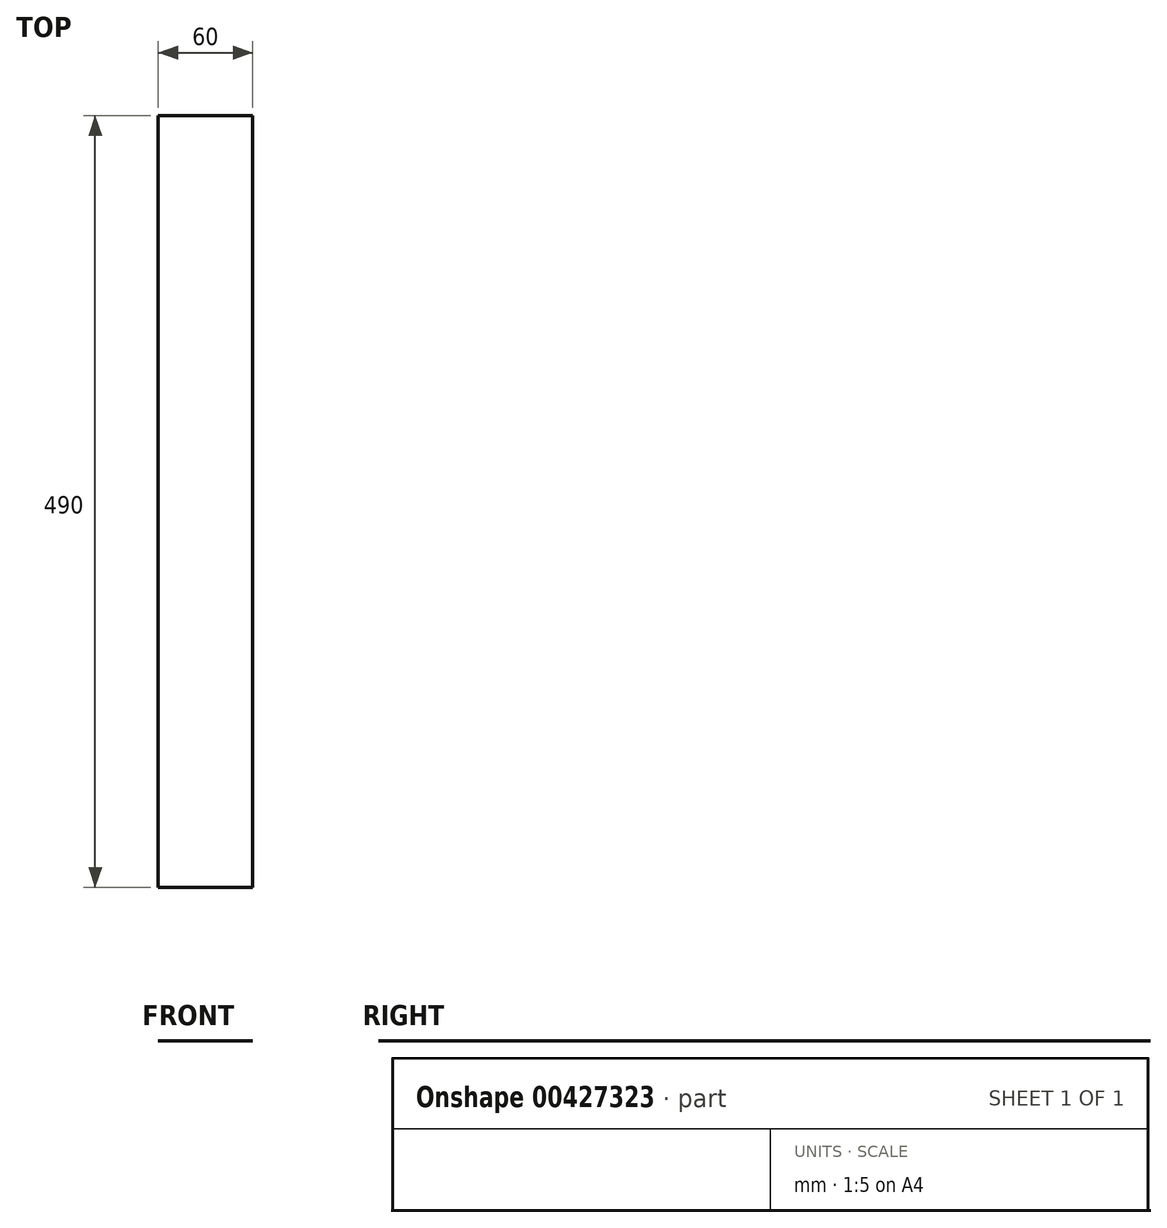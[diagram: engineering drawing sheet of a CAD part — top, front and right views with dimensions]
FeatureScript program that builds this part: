
annotation { "Feature Type Name" : "Feature", "Feature Type Description" : "" }
export const myFeature = defineFeature(function(context is Context, id is Id, definition is map)
    precondition{}
    {
        {
            var Q0;
            Q0=qCreatedBy(makeId("Top.planeOp"),FACE);
            var sketch = newSketch(context, id + "F0", { "sketchPlane" : qUnion([Q0])});
            skLineSegment(sketch, "E0.bottom", {"start": v(30, -245) * mm, "end": v(-30, -245) * mm});
            skLineSegment(sketch, "E0.top", {"start": v(30, 245) * mm, "end": v(-30, 245) * mm});
            skLineSegment(sketch, "E0.left", {"start": v(30, -245) * mm, "end": v(30, 245) * mm});
            skLineSegment(sketch, "E0.right", {"start": v(-30, -245) * mm, "end": v(-30, 245) * mm});
            skPoint(sketch, "E0.middle", {"position": v(0, 0) * mm});
            skSolve(sketch);
        }
        {
            var Q0;
            Q0 = qSketchRegion(id + "F0", true);
            extrude(context, id + "F1", {"entities" : qUnion([Q0]), "depth" : 1 / 812.8 * mm});
        }
    });
